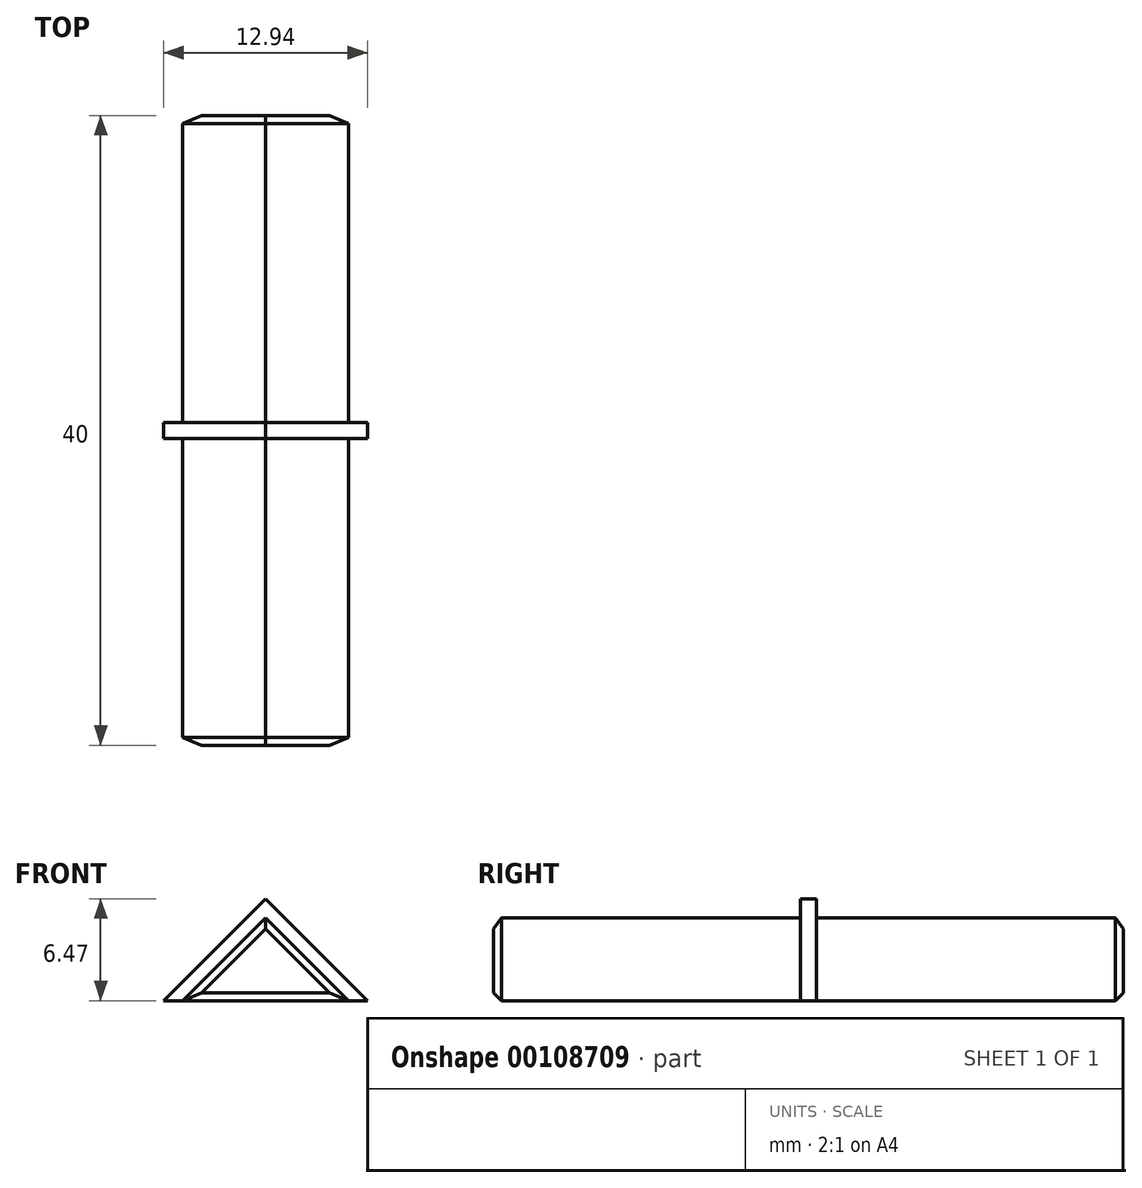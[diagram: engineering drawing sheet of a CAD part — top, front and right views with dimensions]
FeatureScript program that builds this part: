
annotation { "Feature Type Name" : "Feature", "Feature Type Description" : "" }
export const myFeature = defineFeature(function(context is Context, id is Id, definition is map)
    precondition{}
    {
        {
            var Q0;
            Q0=qCreatedBy(makeId("Front.planeOp"),FACE);
            var sketch = newSketch(context, id + "F0", { "sketchPlane" : qUnion([Q0])});
            skLineSegment(sketch, "E0", {"start": v(0, 0) * mm, "end": v(0, 7.45) * mm});
            skLineSegment(sketch, "E1", {"start": v(0, 0) * mm, "end": v(7.45, 0) * mm});
            skLineSegment(sketch, "E2", {"start": v(7.45, 0) * mm, "end": v(0, 7.45) * mm});
            skLineSegment(sketch, "E3.0", {"start": v(-0.85, -0.85) * mm, "end": v(-0.85, 8.3) * mm});
            skLineSegment(sketch, "E3.1", {"start": v(-0.85, -0.85) * mm, "end": v(8.3, -0.85) * mm});
            skLineSegment(sketch, "E4", {"start": v(-0.85, 8.3) * mm, "end": v(0, 7.45) * mm});
            skLineSegment(sketch, "E5", {"start": v(8.3, -0.85) * mm, "end": v(7.45, 0) * mm});
            skSolve(sketch);
        }
        {
            var Q0;
            Q0=makeQuery(id+"F0.imprint","IMPRINT",FACE,{"disambiguationData":[TD([[makeQuery(id+"F0.imprint","IMPRINT",EDGE,{"derivedFrom":sQuery(id+"F0.wireOp",EDGE,"E0")}),-1.0]])]});
            extrude(context, id + "F1", {"entities" : qUnion([Q0]), "depth" : 20 * mm, "hasSecondDirection" : true, "secondDirectionOppositeDirection" : true, "secondDirectionDepth" : 20 * mm});
        }
        {
            var Q0;
            Q0=makeQuery(id+"F1.opExtrude","CAP_EDGE",EDGE,{"disambiguationData":[OSD([sQuery(id+"F0.wireOp",EDGE,"E2")])],"isStart":false});
            var Q1;
            Q1=makeQuery(id+"F1.opExtrude","CAP_EDGE",EDGE,{"disambiguationData":[OSD([sQuery(id+"F0.wireOp",EDGE,"E0")])],"isStart":false});
            var Q2;
            Q2=makeQuery(id+"F1.opExtrude","CAP_EDGE",EDGE,{"disambiguationData":[OSD([sQuery(id+"F0.wireOp",EDGE,"E1")])],"isStart":false});
            var Q3;
            Q3=makeQuery(id+"F1.opExtrude","CAP_EDGE",EDGE,{"disambiguationData":[OSD([sQuery(id+"F0.wireOp",EDGE,"E2")])],"isStart":true});
            var Q4;
            Q4=makeQuery(id+"F1.opExtrude","CAP_EDGE",EDGE,{"disambiguationData":[OSD([sQuery(id+"F0.wireOp",EDGE,"E0")])],"isStart":true});
            var Q5;
            Q5=makeQuery(id+"F1.opExtrude","CAP_EDGE",EDGE,{"disambiguationData":[OSD([sQuery(id+"F0.wireOp",EDGE,"E1")])],"isStart":true});
            chamfer(context, id + "F2", {"entities" : qUnion([Q0, Q1, Q2, Q3, Q4, Q5]), "width" : .5 * mm, "tangentPropagation" : true});
        }
        {
            var Q0;
            Q0=makeQuery(id+"F0.imprint","IMPRINT",FACE,{"disambiguationData":[TD([[makeQuery(id+"F0.imprint","IMPRINT",EDGE,{"derivedFrom":sQuery(id+"F0.wireOp",EDGE,"E0")}),1.0]])]});
            extrude(context, id + "F3", {"entities" : qUnion([Q0]), "operationType" : NewBodyOperationType.ADD, "depth" : .5 * mm, "hasSecondDirection" : true, "secondDirectionOppositeDirection" : true, "secondDirectionDepth" : .5 * mm});
        }
        {
            var Q0;
            Q0=makeQuery(id+"F1.opExtrude","SWEPT_BODY",BODY,{"disambiguationData":[OSD([sQuery(id+"F0.wireOp",EDGE,"E0"),sQuery(id+"F0.wireOp",EDGE,"E1"),sQuery(id+"F0.wireOp",EDGE,"E2")])]});
            var Q1;
            {var subQ0=sQuery(id+"F0.wireOp",EDGE,"E2");var subQ1=sQuery(id+"F0.wireOp",EDGE,"E5");var subQ2=sQuery(id+"F0.wireOp",EDGE,"E1");Q1=makeQuery(id+"F3.boolean.opBoolean","SPLIT",EDGE,{"disambiguationData":[TD([makeQuery(id+"F2.opChamfer","BLEND_FACE",FACE,{"disambiguationData":[OSD([subQ2]),TDD([makeQuery(id+"F1.opExtrude","CAP_EDGE",EDGE,{"disambiguationData":[OSD([subQ2])],"isStart":false})])]})])],"derivedFrom":makeQuery(id+"F1.opExtrude","SWEPT_EDGE",EDGE,{"disambiguationData":[OSD([subQ2,subQ0,subQ1])]})});}
            transform(context, id + "F4", {"entities" : qUnion([Q0]), "transformType" : TransformType.ROTATION, "transformAxis" : qUnion([Q1]), "angle" : 135 * degree, "makeCopy" : false});
        }
    });
